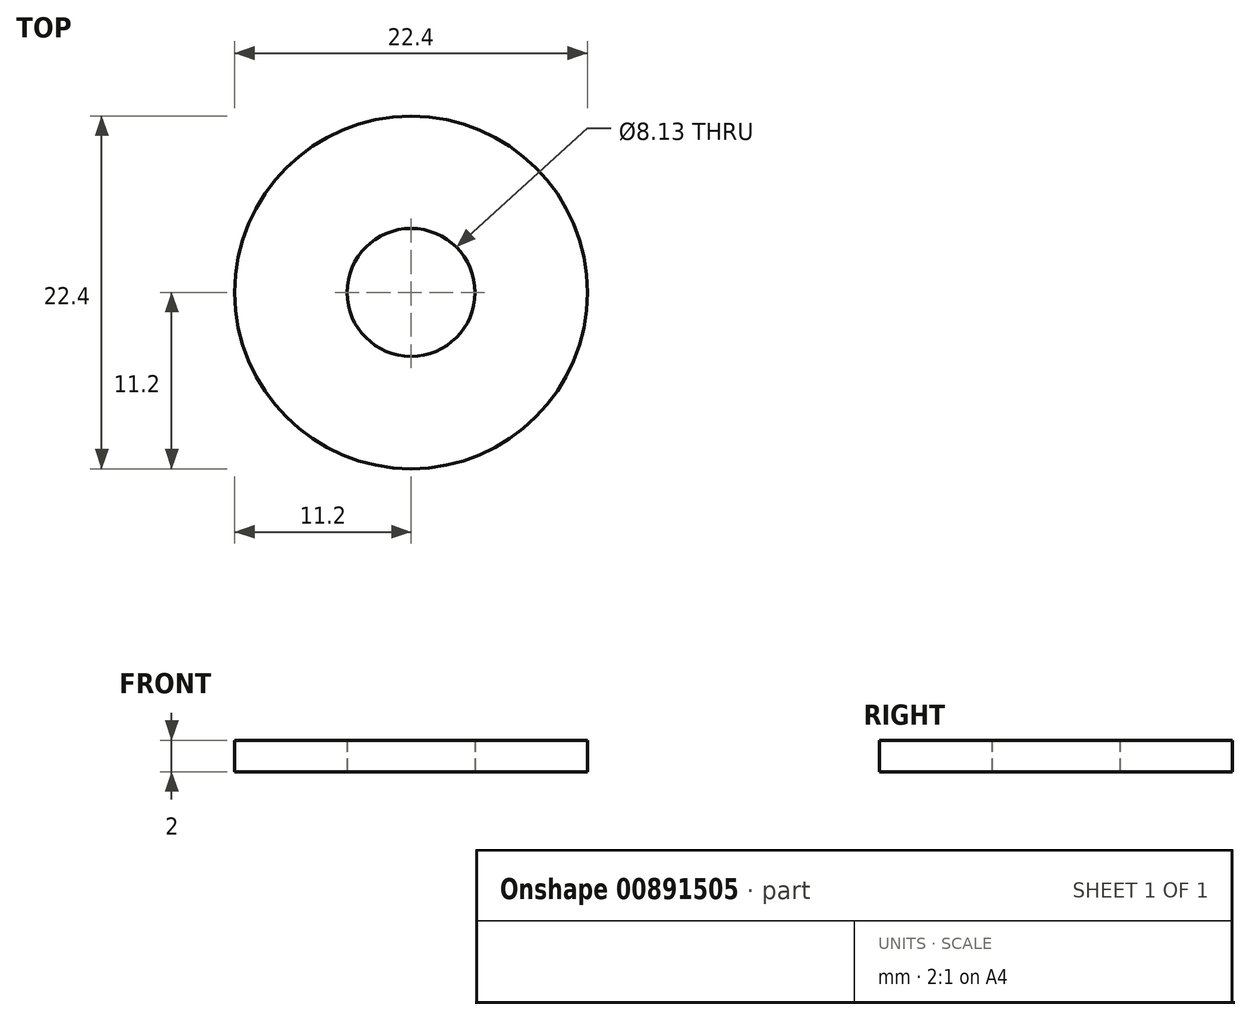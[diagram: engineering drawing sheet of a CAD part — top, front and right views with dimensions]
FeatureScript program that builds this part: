
annotation { "Feature Type Name" : "Feature", "Feature Type Description" : "" }
export const myFeature = defineFeature(function(context is Context, id is Id, definition is map)
    precondition{}
    {
        {
            var Q0;
            Q0=qCreatedBy(makeId("Top.planeOp"),FACE);
            var sketch = newSketch(context, id + "F0", { "sketchPlane" : qUnion([Q0])});
            skCircle(sketch, "E0", {"center": v(0, 0) * mm, "radius": 11.2 * mm});
            skCircle(sketch, "E1", {"center": v(0, 0) * mm, "radius": 4.06 * mm});
            skSolve(sketch);
        }
        {
            var Q0;
            Q0 = qSketchRegion(id + "F0", true);
            extrude(context, id + "F1", {"entities" : qUnion([Q0]), "depth" : 2 * mm, "offsetDistance" : 25 * mm});
        }
    });
